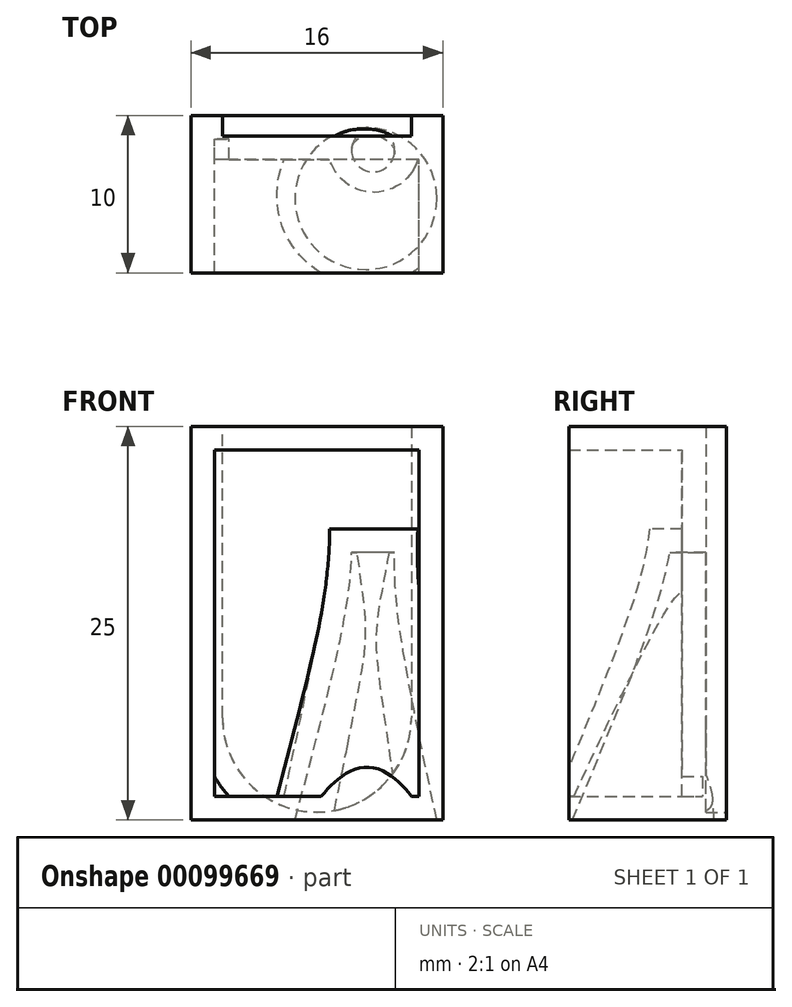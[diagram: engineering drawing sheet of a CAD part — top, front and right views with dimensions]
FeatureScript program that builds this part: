
annotation { "Feature Type Name" : "Feature", "Feature Type Description" : "" }
export const myFeature = defineFeature(function(context is Context, id is Id, definition is map)
    precondition{}
    {
        {
            var Q0;
            Q0=qCreatedBy(makeId("Top.planeOp"),FACE);
            var sketch = newSketch(context, id + "F0", { "sketchPlane" : qUnion([Q0])});
            skLineSegment(sketch, "E0.bottom", {"start": v(8, -5) * mm, "end": v(-8, -5) * mm});
            skLineSegment(sketch, "E0.top", {"start": v(8, 5) * mm, "end": v(-8, 5) * mm});
            skLineSegment(sketch, "E0.left", {"start": v(8, -5) * mm, "end": v(8, 5) * mm});
            skLineSegment(sketch, "E0.right", {"start": v(-8, -5) * mm, "end": v(-8, 5) * mm});
            skPoint(sketch, "E0.middle", {"position": v(0, 0) * mm});
            skSolve(sketch);
        }
        {
            var Q0;
            Q0=makeQuery(id+"F0.imprint","IMPRINT",FACE,{"disambiguationData":[TD([[makeQuery(id+"F0.imprint","IMPRINT",EDGE,{"derivedFrom":sQuery(id+"F0.wireOp",EDGE,"E0.bottom")}),-1.0]])]});
            extrude(context, id + "F1", {"entities" : qUnion([Q0]), "depth" : 25 * mm});
        }
        {
            var Q0;
            Q0=makeQuery(id+"F1.opExtrude","SWEPT_FACE",FACE,{"disambiguationData":[OSD([sQuery(id+"F0.wireOp",EDGE,"E0.top")])]});
            var sketch = newSketch(context, id + "F2", { "sketchPlane" : qUnion([Q0])});
            skLineSegment(sketch, "E1", {"start": v(-6, 25) * mm, "end": v(-6, 6.5) * mm});
            skArc(sketch, "E2", {"start": v(-6, 6.5) * mm, "mid": v(0, 0.5) * mm, "end": v(6, 6.5) * mm});
            skLineSegment(sketch, "E3", {"start": v(6, 6.5) * mm, "end": v(6, 25) * mm});
            skSolve(sketch);
        }
        {
            var Q0;
            {var subQ0=sQuery(id+"F2.wireOp",EDGE,"E1");Q0=makeQuery(id+"F2.imprint","IMPRINT",FACE,{"disambiguationData":[TD([[makeQuery(id+"F2.imprint","IMPRINT",EDGE,{"derivedFrom":subQ0}),1.0]])]});}
            extrude(context, id + "F3", {"entities" : qUnion([Q0]), "operationType" : NewBodyOperationType.REMOVE, "oppositeDirection" : true, "depth" : 1.3 * mm});
        }
        {
            var Q0;
            Q0=makeQuery(id+"F1.opExtrude","CAP_FACE",FACE,{"disambiguationData":[OSD([sQuery(id+"F0.wireOp",EDGE,"E0.bottom"),sQuery(id+"F0.wireOp",EDGE,"E0.top"),sQuery(id+"F0.wireOp",EDGE,"E0.left"),sQuery(id+"F0.wireOp",EDGE,"E0.right")])],"isStart":true});
            var sketch = newSketch(context, id + "F4", { "sketchPlane" : qUnion([Q0])});
            skCircle(sketch, "E4", {"center": v(3.11, 0.27) * mm, "radius": 4.5 * mm});
            skSolve(sketch);
        }
        {
            var Q0;
            Q0=makeQuery(id+"F4.imprint","IMPRINT",FACE,{"disambiguationData":[TD([[makeQuery(id+"F4.imprint","IMPRINT",EDGE,{"derivedFrom":sQuery(id+"F4.wireOp",EDGE,"E4")}),-1.0]])]});
            cPlane(context, id + "F5", {"entities" : qUnion([Q0]), "cplaneType" : CPlaneType.OFFSET, "offset" : 17 * mm, "oppositeDirection" : true, "width" : 150 * mm, "height" : 150 * mm});
        }
        {
            var Q0;
            Q0=qCreatedBy(id+"F5.planeOp",FACE);
            var sketch = newSketch(context, id + "F6", { "sketchPlane" : qUnion([Q0])});
            skCircle(sketch, "E5", {"center": v(3.57, -2.78) * mm, "radius": 1.37 * mm});
            skSolve(sketch);
        }
        {
            var Q1;
            Q1 = qSketchRegion(id + "F6", true);
            var Q2;
            Q2 = qSketchRegion(id + "F4", true);
            loft(context, id + "F7", {"operationType" : NewBodyOperationType.REMOVE, "sheetProfilesArray" : [{ "sheetProfileEntities" : qUnion([Q1]) }, { "sheetProfileEntities" : qUnion([Q2]) }]});
        }
        {
            var Q0;
            Q0=makeQuery(id+"F1.opExtrude","SWEPT_FACE",FACE,{"disambiguationData":[OSD([sQuery(id+"F0.wireOp",EDGE,"E0.bottom")])]});
            shell(context, id + "F8", {"entities" : qUnion([Q0]), "thickness" : 1.5 * mm});
        }
    });
